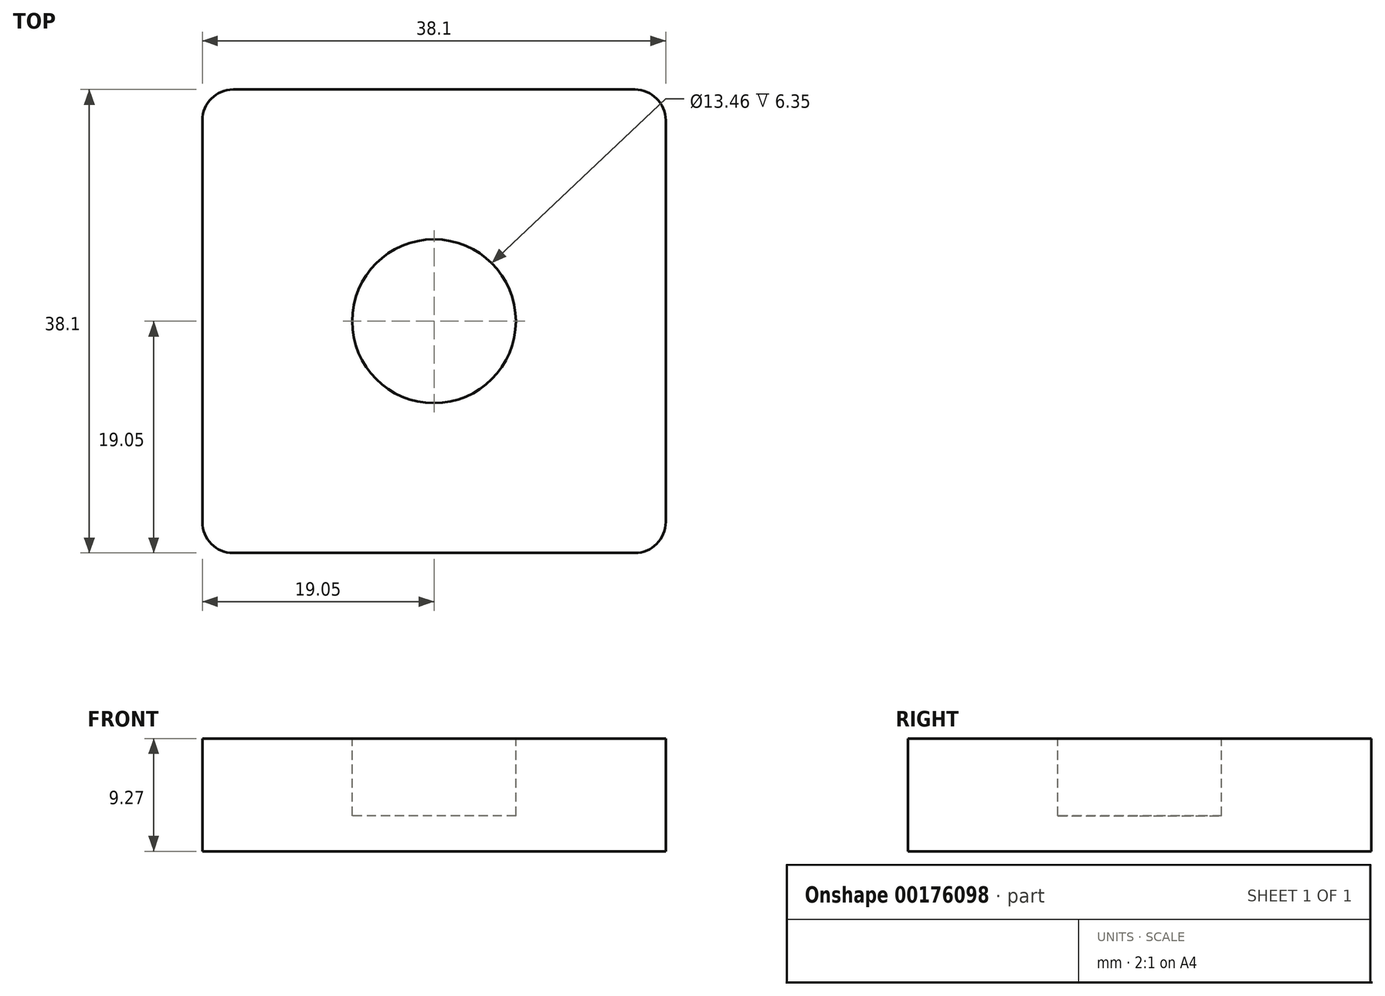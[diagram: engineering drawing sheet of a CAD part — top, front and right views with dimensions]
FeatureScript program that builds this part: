
annotation { "Feature Type Name" : "Feature", "Feature Type Description" : "" }
export const myFeature = defineFeature(function(context is Context, id is Id, definition is map)
    precondition{}
    {
        {
            var Q0;
            Q0=qCreatedBy(makeId("Top.planeOp"),FACE);
            var sketch = newSketch(context, id + "F0", { "sketchPlane" : qUnion([Q0])});
            skLineSegment(sketch, "E0.bottom", {"start": v(-16.51, 19.05) * mm, "end": v(16.5, 19.05) * mm});
            skLineSegment(sketch, "E0.top", {"start": v(-16.51, -19.05) * mm, "end": v(16.51, -19.05) * mm});
            skLineSegment(sketch, "E0.left", {"start": v(-19.05, 16.5) * mm, "end": v(-19.05, -16.51) * mm});
            skLineSegment(sketch, "E0.right", {"start": v(19.05, 16.51) * mm, "end": v(19.05, -16.51) * mm});
            skPoint(sketch, "E1.visualSharp", {"position": v(-19.05, 19.05) * mm});
            skArc(sketch, "E1.filletArc", {"start": v(-16.51, 19.05) * mm, "mid": v(-18.3, 18.3) * mm, "end": v(-19.05, 16.51) * mm});
            skPoint(sketch, "E2.visualSharp", {"position": v(19.05, 19.05) * mm});
            skArc(sketch, "E2.filletArc", {"start": v(19.05, 16.51) * mm, "mid": v(18.3, 18.3) * mm, "end": v(16.5, 19.05) * mm});
            skPoint(sketch, "E3.visualSharp", {"position": v(19.05, -19.05) * mm});
            skArc(sketch, "E3.filletArc", {"start": v(16.51, -19.05) * mm, "mid": v(18.3, -18.3) * mm, "end": v(19.05, -16.51) * mm});
            skPoint(sketch, "E4.visualSharp", {"position": v(-19.05, -19.05) * mm});
            skArc(sketch, "E4.filletArc", {"start": v(-19.05, -16.51) * mm, "mid": v(-18.3, -18.3) * mm, "end": v(-16.51, -19.05) * mm});
            skSolve(sketch);
        }
        {
            var Q0;
            Q0=makeQuery(id+"F0.imprint","IMPRINT",FACE,{"disambiguationData":[TD([[makeQuery(id+"F0.imprint","IMPRINT",EDGE,{"derivedFrom":sQuery(id+"F0.wireOp",EDGE,"E0.bottom")}),-1.0]])]});
            extrude(context, id + "F1", {"entities" : qUnion([Q0]), "depth" : 9.27 * mm});
        }
        {
            var Q0;
            Q0=makeQuery(id+"F1.opExtrude","CAP_FACE",FACE,{"disambiguationData":[OSD([sQuery(id+"F0.wireOp",EDGE,"E0.bottom"),sQuery(id+"F0.wireOp",EDGE,"E0.top"),sQuery(id+"F0.wireOp",EDGE,"E0.left"),sQuery(id+"F0.wireOp",EDGE,"E0.right"),sQuery(id+"F0.wireOp",EDGE,"E1.filletArc"),sQuery(id+"F0.wireOp",EDGE,"E2.filletArc"),sQuery(id+"F0.wireOp",EDGE,"E3.filletArc"),sQuery(id+"F0.wireOp",EDGE,"E4.filletArc")])],"isStart":false});
            var sketch = newSketch(context, id + "F2", { "sketchPlane" : qUnion([Q0])});
            skCircle(sketch, "E5", {"center": v(0, 0) * mm, "radius": 6.73 * mm});
            skSolve(sketch);
        }
        {
            var Q0;
            Q0=qSketchRegion(id+"F2",true);
            var Q1;
            Q1=makeQuery(id+"F2.imprint","IMPRINT",FACE,{"disambiguationData":[TD([[makeQuery(id+"F2.imprint","IMPRINT",EDGE,{"derivedFrom":sQuery(id+"F2.wireOp",EDGE,"E5")}),1.0]])]});
            extrude(context, id + "F3", {"entities" : qUnion([Q0, Q1]), "operationType" : NewBodyOperationType.REMOVE, "oppositeDirection" : true, "depth" : 6.35 * mm});
        }
    });
